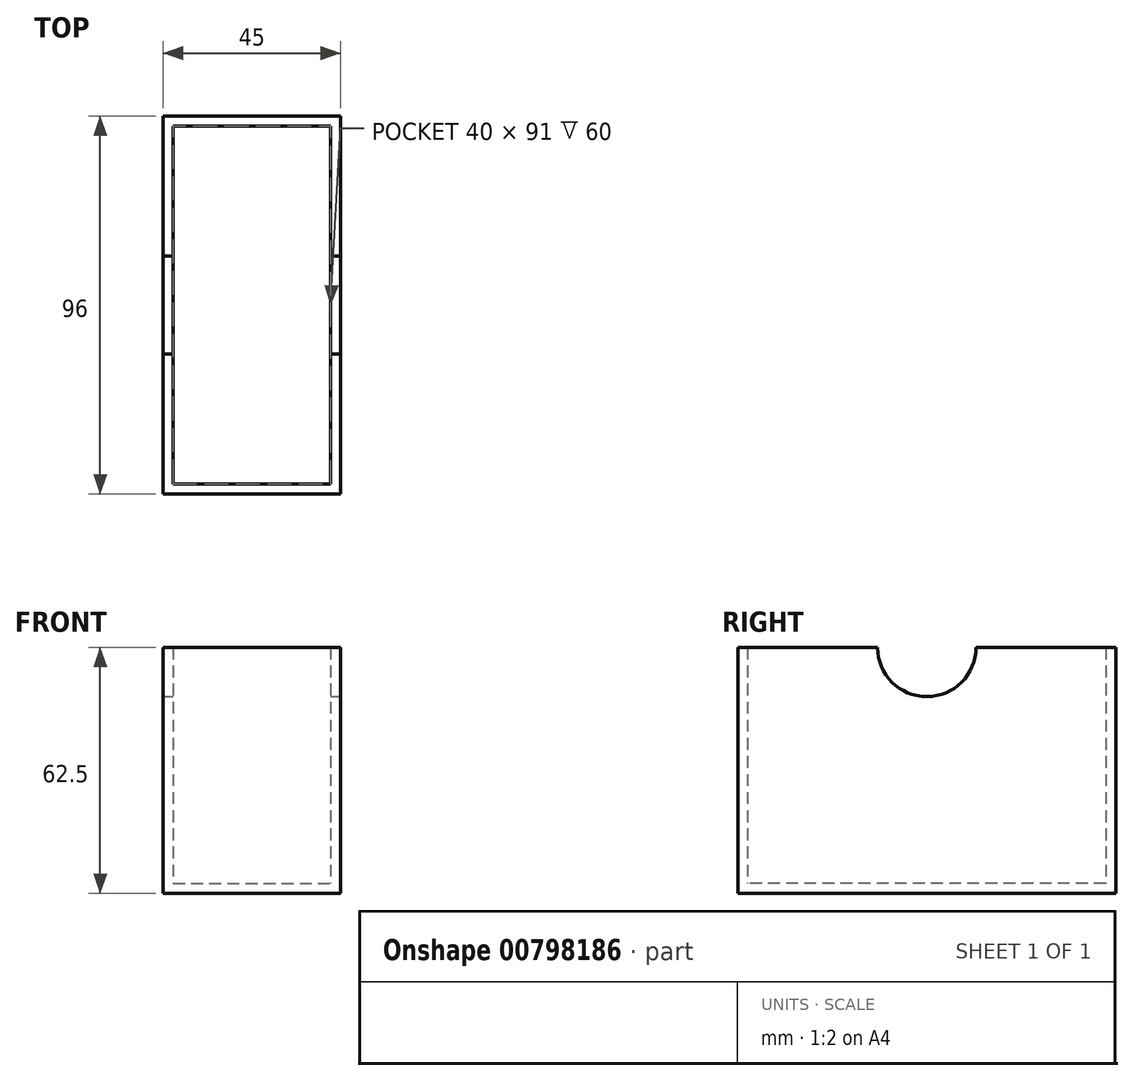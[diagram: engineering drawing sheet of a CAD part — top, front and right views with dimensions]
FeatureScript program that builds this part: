
annotation { "Feature Type Name" : "Feature", "Feature Type Description" : "" }
export const myFeature = defineFeature(function(context is Context, id is Id, definition is map)
    precondition{}
    {
        {
            var Q0;
            Q0=qCreatedBy(makeId("Top.planeOp"),FACE);
            var sketch = newSketch(context, id + "F0", { "sketchPlane" : qUnion([Q0])});
            skLineSegment(sketch, "E0.bottom", {"start": v(-20, 45.5) * mm, "end": v(20, 45.5) * mm});
            skLineSegment(sketch, "E0.top", {"start": v(-20, -45.5) * mm, "end": v(20, -45.5) * mm});
            skLineSegment(sketch, "E0.left", {"start": v(-20, 45.5) * mm, "end": v(-20, -45.5) * mm});
            skLineSegment(sketch, "E0.right", {"start": v(20, 45.5) * mm, "end": v(20, -45.5) * mm});
            skPoint(sketch, "E0.middle", {"position": v(0, 0) * mm});
            skSolve(sketch);
        }
        {
            var Q0;
            Q0=qSketchRegion(id+"F0",true);
            extrude(context, id + "F1", {"entities" : qUnion([Q0]), "depth" : 60 * mm, "offsetDistance" : 25 * mm});
        }
        {
            var Q0;
            Q0=makeQuery(id+"F1.opExtrude","CAP_FACE",FACE,{"disambiguationData":[OSD([sQuery(id+"F0.wireOp",EDGE,"E0.bottom"),sQuery(id+"F0.wireOp",EDGE,"E0.top"),sQuery(id+"F0.wireOp",EDGE,"E0.left"),sQuery(id+"F0.wireOp",EDGE,"E0.right")])],"isStart":false});
            shell(context, id + "F2", {"entities" : qUnion([Q0]), "thickness" : 2.5 * mm, "oppositeDirection" : true});
        }
        {
            var Q0;
            Q0=makeQuery(id+"F1.opExtrude","SWEPT_FACE",FACE,{"disambiguationData":[OSD([sQuery(id+"F0.wireOp",EDGE,"E0.right")])]});
            var sketch = newSketch(context, id + "F3", { "sketchPlane" : qUnion([Q0])});
            skCircle(sketch, "E1", {"center": v(0, 60) * mm, "radius": 12.5 * mm});
            skSolve(sketch);
        }
        {
            var Q0;
            {var subQ0=sQuery(id+"F3.wireOp",EDGE,"E1");var subQ1=makeQuery(id+"F1.opExtrude","CAP_EDGE",EDGE,{"disambiguationData":[OSD([sQuery(id+"F0.wireOp",EDGE,"E0.right")])],"isStart":false});var subQ2=makeQuery(id+"F3.imprint","INTERSECT",VERTEX,{"disambiguationData":[OD(0.0)],"derivedFrom":[subQ1,subQ0]});Q0=makeQuery(id+"F3.imprint","IMPRINT",FACE,{"disambiguationData":[TD([[makeQuery(id+"F3.imprint","IMPRINT",EDGE,{"disambiguationData":[TD([[subQ2,1.0]])],"derivedFrom":subQ0}),1.0]])]});}
            var Q1;
            Q1=sQuery(id+"F3.wireOp",EDGE,"E1");
            extrude(context, id + "F4", {"entities" : qUnion([Q0]), "operationType" : NewBodyOperationType.REMOVE, "surfaceOperationType" : NewSurfaceOperationType.ADD, "surfaceEntities" : qUnion([Q1]), "endBound" : BoundingType.THROUGH_ALL, "oppositeDirection" : true, "depth" : 143 * mm, "offsetDistance" : 25 * mm});
        }
    });
